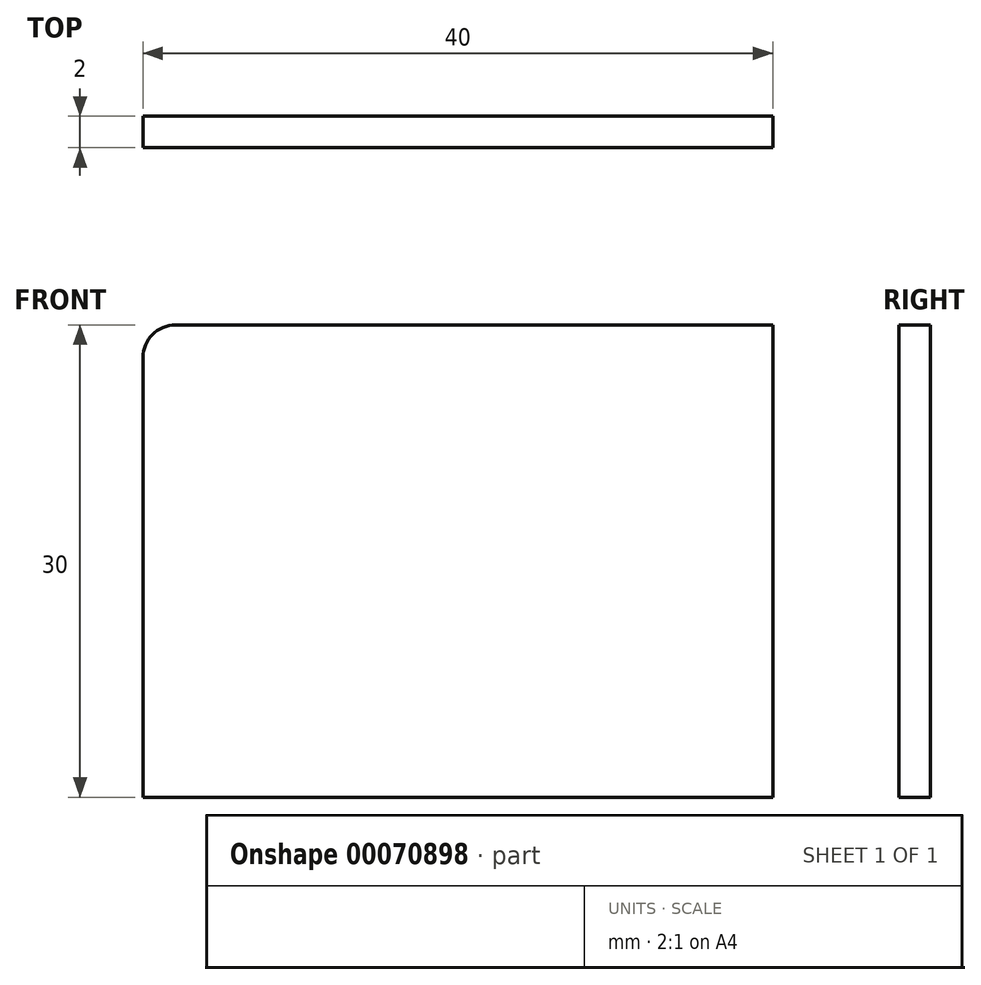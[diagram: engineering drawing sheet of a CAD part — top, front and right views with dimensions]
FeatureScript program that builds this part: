
annotation { "Feature Type Name" : "Feature", "Feature Type Description" : "" }
export const myFeature = defineFeature(function(context is Context, id is Id, definition is map)
    precondition{}
    {
        {
            var Q0;
            Q0=qCreatedBy(makeId("Front.planeOp"),FACE);
            var sketch = newSketch(context, id + "F0", { "sketchPlane" : qUnion([Q0])});
            skLineSegment(sketch, "E0.bottom", {"start": v(-19.72, 0) * mm, "end": v(20.28, 0) * mm});
            skLineSegment(sketch, "E0.top", {"start": v(-17.65, 30) * mm, "end": v(20.28, 30) * mm});
            skLineSegment(sketch, "E0.left", {"start": v(-19.72, 0) * mm, "end": v(-19.72, 27.93) * mm});
            skLineSegment(sketch, "E0.right", {"start": v(20.28, 0) * mm, "end": v(20.28, 30) * mm});
            skPoint(sketch, "E1.visualSharp", {"position": v(-19.72, 30) * mm});
            skArc(sketch, "E1.filletArc", {"start": v(-17.65, 30) * mm, "mid": v(-19.11, 29.4) * mm, "end": v(-19.72, 27.93) * mm});
            skSolve(sketch);
        }
        {
            var Q0;
            Q0 = qSketchRegion(id + "F0", true);
            extrude(context, id + "F1", {"entities" : qUnion([Q0]), "depth" : 2 * mm});
        }
    });
